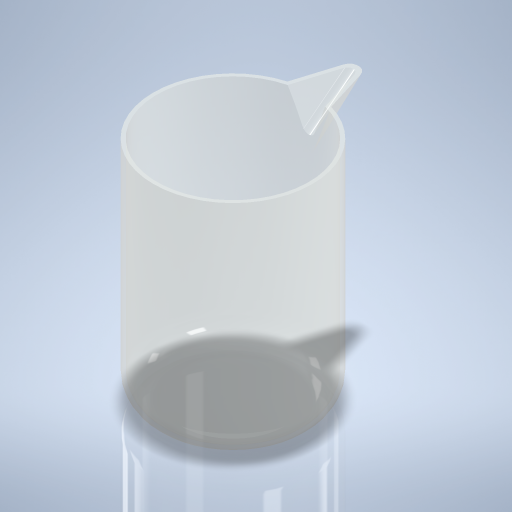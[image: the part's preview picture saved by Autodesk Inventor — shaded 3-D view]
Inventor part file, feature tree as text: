
AUTODESK INVENTOR PART (.ipt)
format: ipt  version: 2024 (Build 280153000, 153)  size: 327,680 bytes
history: native  units: mm
features: sketch x3, fillet x2, extrude x1, plane x1, loft x1, shell x1
ambient origin geometry x8: Origin, YZ Plane, XZ Plane, XY Plane, X Axis, Y Axis, Z Axis, Center Point
bodies: Volumenkörper1 (feature_tree)
feature tree (9):
  extrude  "Extrusion1"  Depth=6.0mm TaperAngle=0.0deg
  fillet  "Rundung1"  Radius=6.0mm
  sketch  "Skizze2"  dims[d5=10.0mm d6=2.0mm d7=10.0mm d24=17.0mm]
  plane  "Arbeitsebene3"
  loft  "Erhebung3"
  shell  "Wandung2"  Thickness=10.0mm
  fillet  "Rundung3"  Radius=17.0mm
  sketch  "Skizze1"  dims[d0=35.0mm d1=50.0mm d2=0.0mm d3=6.0mm]
  sketch  "Skizze6"  dims[d25=0.0mm d26=0.5mm d27=12.0mm d28=0.0mm d29=90.0deg d30=0.0mm d31=90.0deg d32=0.8mm d33=1.5mm]
